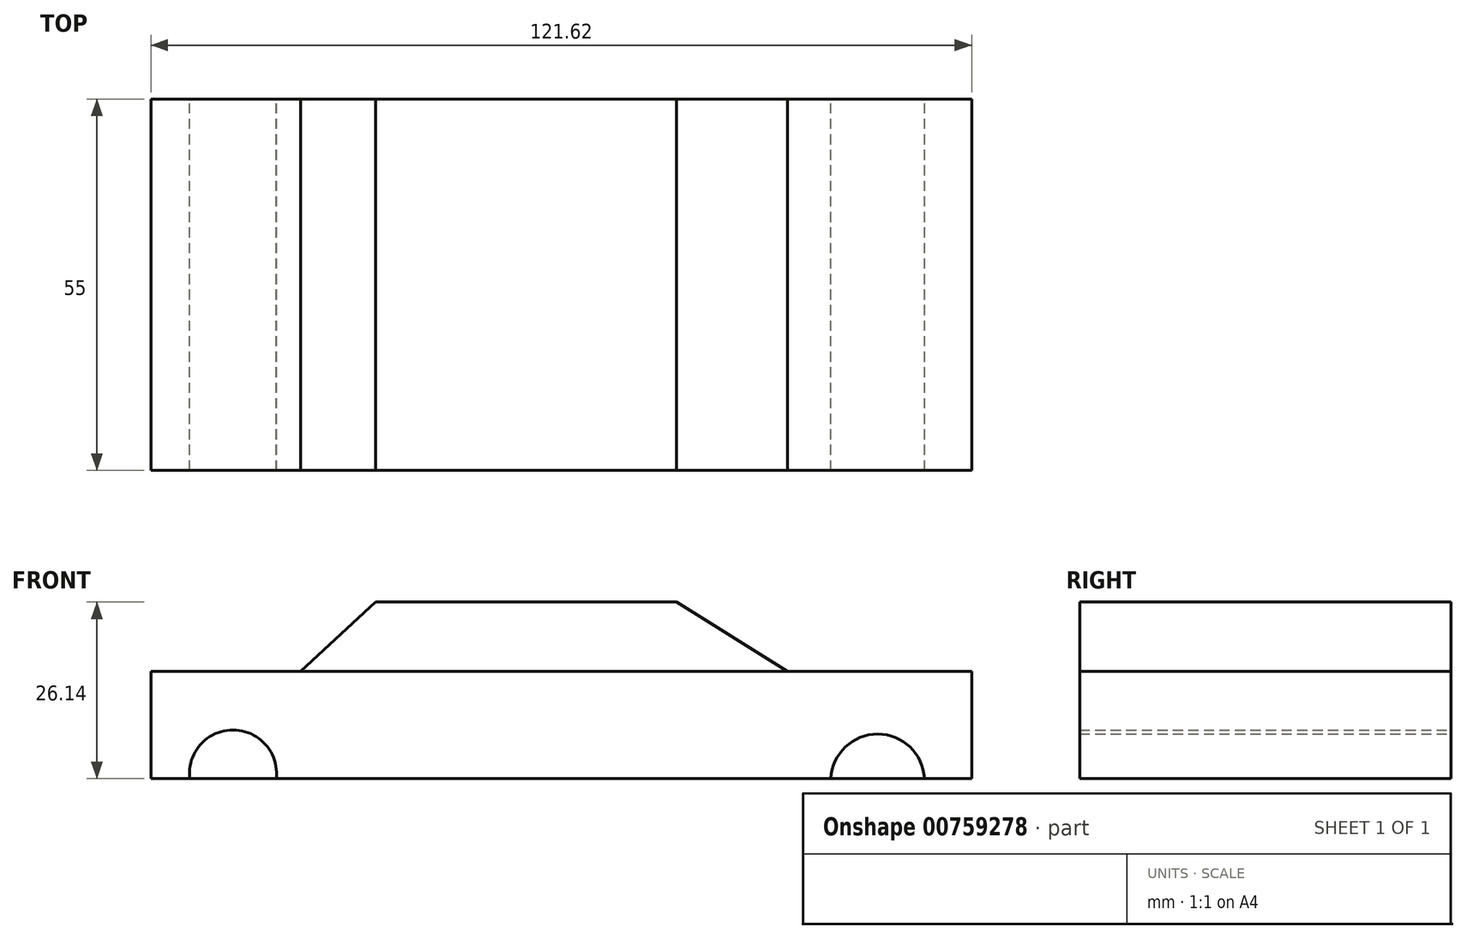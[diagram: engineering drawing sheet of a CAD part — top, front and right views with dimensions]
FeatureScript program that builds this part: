
annotation { "Feature Type Name" : "Feature", "Feature Type Description" : "" }
export const myFeature = defineFeature(function(context is Context, id is Id, definition is map)
    precondition{}
    {
        {
            var Q0;
            Q0=qCreatedBy(makeId("Front.planeOp"),FACE);
            var sketch = newSketch(context, id + "F0", { "sketchPlane" : qUnion([Q0])});
            skLineSegment(sketch, "E0.bottom", {"start": v(-56, 0) * mm, "end": v(65.6, 0) * mm});
            skLineSegment(sketch, "E0.top", {"start": v(-56, 15.9) * mm, "end": v(65.6, 15.9) * mm});
            skLineSegment(sketch, "E0.left", {"start": v(-56, 0) * mm, "end": v(-56, 15.9) * mm});
            skLineSegment(sketch, "E0.right", {"start": v(65.6, 0) * mm, "end": v(65.6, 15.9) * mm});
            skLineSegment(sketch, "E1.bottom", {"start": v(-29.34, 15.9) * mm, "end": v(33.4, 15.9) * mm});
            skLineSegment(sketch, "E1.top", {"start": v(-22.72, 26.14) * mm, "end": v(21.87, 26.14) * mm});
            skLineSegment(sketch, "E2", {"start": v(21.87, 26.14) * mm, "end": v(38.3, 15.9) * mm});
            skLineSegment(sketch, "E3", {"start": v(-22.72, 26.14) * mm, "end": v(-33.82, 15.9) * mm});
            skSolve(sketch);
        }
        {
            var Q0;
            Q0=makeQuery(id+"F0.imprint","IMPRINT",FACE,{"disambiguationData":[TD([[makeQuery(id+"F0.imprint","IMPRINT",EDGE,{"derivedFrom":sQuery(id+"F0.wireOp",EDGE,"E0.bottom")}),1.0]])]});
            var sketch = newSketch(context, id + "F1", { "sketchPlane" : qUnion([Q0])});
            skArc(sketch, "E4", {"start": v(58.6, 0) * mm, "mid": v(51.67, 6.58) * mm, "end": v(44.74, 0) * mm});
            skArc(sketch, "E5", {"start": v(-37.42, 0) * mm, "mid": v(-43.83, 7.2) * mm, "end": v(-50.24, 0) * mm});
            skSolve(sketch);
        }
        {
            var Q0;
            {var subQ9=sQuery(id+"F1.wireOp",EDGE,"E4");Q0=makeQuery(id+"F1.imprint","IMPRINT",FACE,{"disambiguationData":[TD([[makeQuery(id+"F1.imprint","IMPRINT",EDGE,{"derivedFrom":subQ9}),-1.0]])]});}
            var Q1;
            Q1=makeQuery(id+"F0.imprint","IMPRINT",FACE,{"disambiguationData":[TD([[makeQuery(id+"F0.imprint","IMPRINT",EDGE,{"derivedFrom":sQuery(id+"F0.wireOp",EDGE,"E0.bottom")}),1.0]])]});
            var Q2;
            Q2=makeQuery(id+"F0.imprint","IMPRINT",FACE,{"disambiguationData":[TD([[makeQuery(id+"F0.imprint","IMPRINT",EDGE,{"derivedFrom":sQuery(id+"F0.wireOp",EDGE,"E1.top")}),-1.0]])]});
            extrude(context, id + "F2", {"entities" : qUnion([Q0, Q1, Q2]), "depth" : 55 * mm, "offsetDistance" : 25 * mm});
        }
    });
